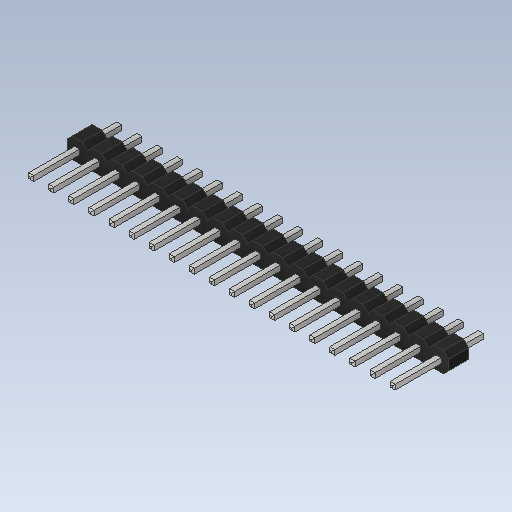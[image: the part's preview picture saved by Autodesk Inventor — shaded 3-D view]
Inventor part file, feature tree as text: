
AUTODESK INVENTOR PART (.ipt)
format: ipt  version: 2020 (Build 240168000, 168)  size: 356,864 bytes
history: imported  units: in
note: dims shown in document units (in); Inventor stores cm internally (conversion verified against a paired STEP export)
features: imported_body x1
ambient origin geometry x8: Origin, YZ Plane, XZ Plane, XY Plane, X Axis, Y Axis, Z Axis, Center Point
bodies: Solid1 (imported_parasolid), Body2 (imported_parasolid)
feature tree (1):
  imported_body  NMx_Import_Brep_tag  [imported B-rep: ~460 faces, bbox_mm=[48.26, 2.54, 11.54]]
